# Revit family: QF_ELECTROLUXPROFESSIONAL_391140_E9BRGJDPF0
name_source: partatom
category: Specialty Equipment
revit_build: Autodesk Revit 2018 (Build: 20190510_1515(x64)
units: mm (PartAtom-declared; Revit-internal decimal feet)

## family parameters
Always vertical = Yes
Cut with Voids When Loaded = No
Part Type = Normal
Room Calculation Point = No
Round Connector Dimension = Use Diameter
Shared = No
Work Plane-Based = No

## types (1)
- QF_ELECTROLUXPROFESSIONAL_391140_E9BRGJDPF0
    Apparent Power = 250 VA
    Cold Water Connection Height = 0 mm  [stored 0 ft]
    Cold Water Maximum Pressure = 0.00 psi
    Cold Water Minimum Pressure = 0.00 psi
    Cold Water Size = 1"
    Conn Conduit = Yes
    Depth = 915 mm  [stored 3.00197 ft]
    Description = 900XP GAS BRATT PAN – 100 LITER WITH DUOMAT BOTTOM
    Direct Waste Size = 0"
    FL Amps = 1 A
    Gas Input = 92043.0 Btu/h
    Gas KW = 27
    Gas Size = 1"
    HP = 0.1 HP
    Height = 850 mm  [stored 2.78871 ft]
    Manufacturer = ELECTROLUX
    Max Overcurrent Protection = 0 A
    Min Ckt Ampacity = 0 A
    Model = 391140
    Phase = 1
    URL = www.electrolux.com
    URL Cutsheet = www.electrolux.com
    Volts = 230 V
    Watts = 250 W
    Weight in Pounds = 180
    Width = 1000 mm  [stored 3.28084 ft]

note: [stored X ft] marks values corroborated as IEEE doubles in the binary element streams (Revit-internal decimal feet)

## geometry (parser evidence)
native form markers: Blend x14, Sweep x1
no freeform markers — native parametric forms only
